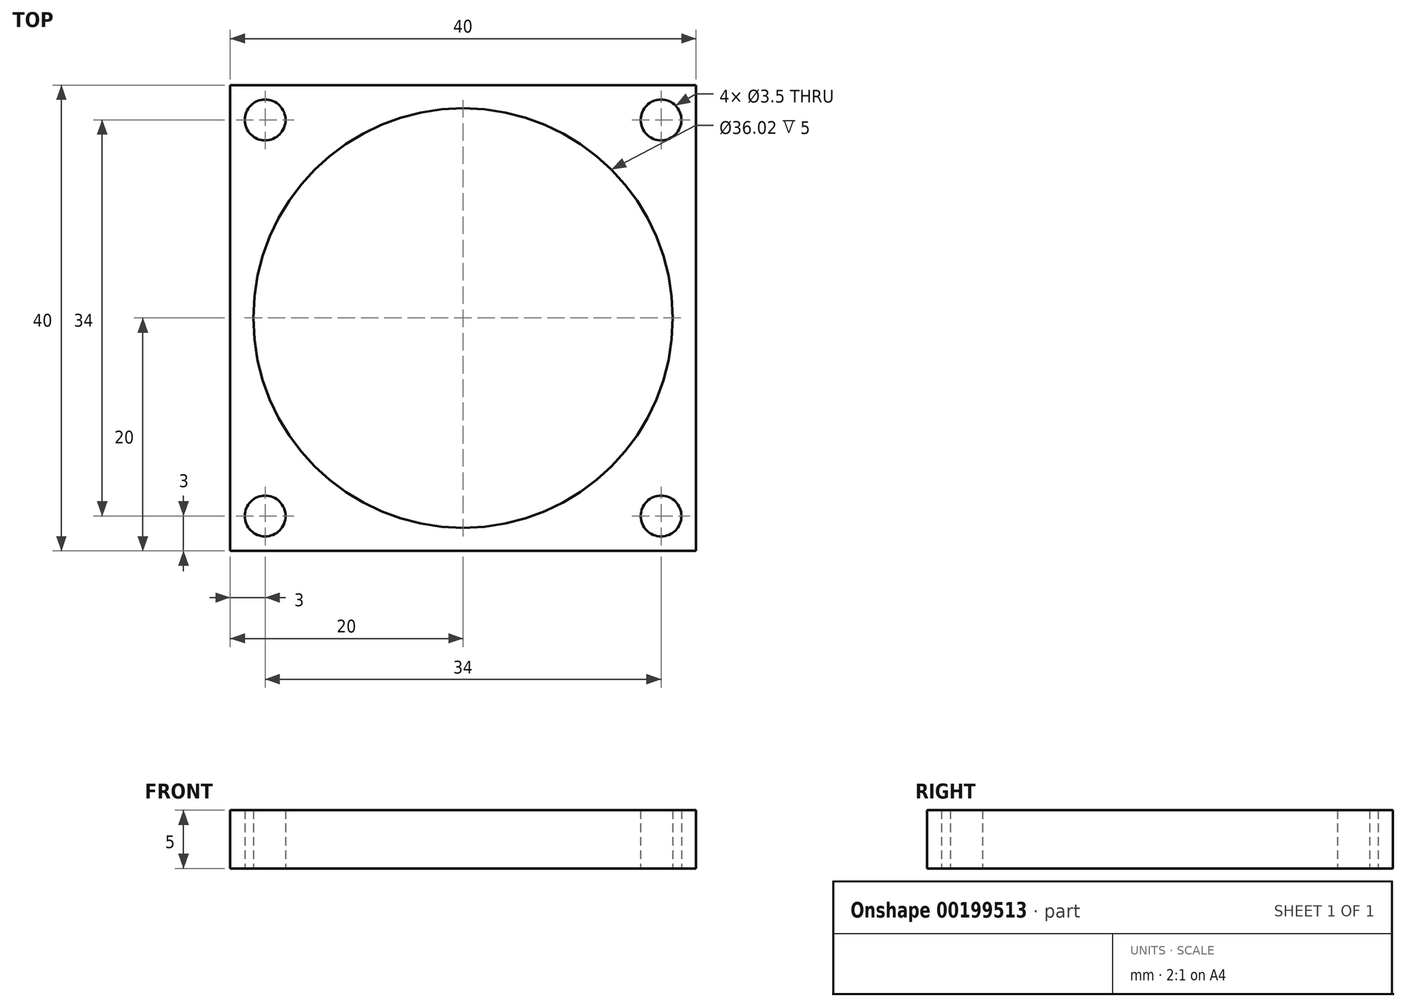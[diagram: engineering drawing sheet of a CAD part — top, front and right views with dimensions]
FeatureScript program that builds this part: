
annotation { "Feature Type Name" : "Feature", "Feature Type Description" : "" }
export const myFeature = defineFeature(function(context is Context, id is Id, definition is map)
    precondition{}
    {
        {
            var Q0;
            Q0=qCreatedBy(makeId("Top.planeOp"),FACE);
            var sketch = newSketch(context, id + "F0", { "sketchPlane" : qUnion([Q0])});
            skLineSegment(sketch, "E0.bottom", {"start": v(20, 20) * mm, "end": v(-20, 20) * mm});
            skLineSegment(sketch, "E0.top", {"start": v(20, -20) * mm, "end": v(-20, -20) * mm});
            skLineSegment(sketch, "E0.left", {"start": v(20, 20) * mm, "end": v(20, -20) * mm});
            skLineSegment(sketch, "E0.right", {"start": v(-20, 20) * mm, "end": v(-20, -20) * mm});
            skPoint(sketch, "E0.middle", {"position": v(0, 0) * mm});
            skLineSegment(sketch, "E1.bottom", {"start": v(17, 17) * mm, "end": v(-17, 17) * mm});
            skLineSegment(sketch, "E1.top", {"start": v(17, -17) * mm, "end": v(-17, -17) * mm});
            skLineSegment(sketch, "E1.left", {"start": v(17, 17) * mm, "end": v(17, -17) * mm});
            skLineSegment(sketch, "E1.right", {"start": v(-17, 17) * mm, "end": v(-17, -17) * mm});
            skCircle(sketch, "E2", {"center": v(-17, 17) * mm, "radius": 1.75 * mm});
            skCircle(sketch, "E3", {"center": v(17, 17) * mm, "radius": 1.75 * mm});
            skCircle(sketch, "E4", {"center": v(17, -17) * mm, "radius": 1.75 * mm});
            skCircle(sketch, "E5", {"center": v(-17, -17) * mm, "radius": 1.75 * mm});
            skCircle(sketch, "E6", {"center": v(0, 0) * mm, "radius": 18.01 * mm});
            skSolve(sketch);
        }
        {
            var Q0;
            Q0 = qSketchRegion(id + "F0", true);
            var Q1;
            {var subQ0=sQuery(id+"F0.wireOp",EDGE,"E6");var subQ1=sQuery(id+"F0.wireOp",EDGE,"E1.top");var subQ2=makeQuery(id+"F0.imprint","INTERSECT",VERTEX,{"disambiguationData":[OD(1.0)],"derivedFrom":[subQ1,subQ0]});Q1=makeQuery(id+"F0.imprint","IMPRINT",FACE,{"disambiguationData":[TD([[makeQuery(id+"F0.imprint","IMPRINT",EDGE,{"disambiguationData":[TD([[subQ2,-1.0]])],"derivedFrom":subQ1}),-1.0]])]});}
            var Q2;
            {var subQ0=sQuery(id+"F0.wireOp",EDGE,"E6");var subQ1=sQuery(id+"F0.wireOp",EDGE,"E1.bottom");var subQ2=makeQuery(id+"F0.imprint","INTERSECT",VERTEX,{"disambiguationData":[OD(1.0)],"derivedFrom":[subQ1,subQ0]});Q2=makeQuery(id+"F0.imprint","IMPRINT",FACE,{"disambiguationData":[TD([[makeQuery(id+"F0.imprint","IMPRINT",EDGE,{"disambiguationData":[TD([[subQ2,-1.0]])],"derivedFrom":subQ1}),1.0]])]});}
            var Q3;
            {var subQ0=sQuery(id+"F0.wireOp",EDGE,"E3");var subQ1=sQuery(id+"F0.wireOp",EDGE,"E1.bottom");var subQ2=makeQuery(id+"F0.imprint","INTERSECT",VERTEX,{"derivedFrom":[subQ1,subQ0]});Q3=makeQuery(id+"F0.imprint","IMPRINT",FACE,{"disambiguationData":[TD([[makeQuery(id+"F0.imprint","IMPRINT",EDGE,{"disambiguationData":[TD([[subQ2,-1.0]])],"derivedFrom":subQ1}),1.0]])]});}
            var Q4;
            {var subQ0=sQuery(id+"F0.wireOp",EDGE,"E4");var subQ1=sQuery(id+"F0.wireOp",EDGE,"E1.top");var subQ2=makeQuery(id+"F0.imprint","INTERSECT",VERTEX,{"derivedFrom":[subQ1,subQ0]});Q4=makeQuery(id+"F0.imprint","IMPRINT",FACE,{"disambiguationData":[TD([[makeQuery(id+"F0.imprint","IMPRINT",EDGE,{"disambiguationData":[TD([[subQ2,-1.0]])],"derivedFrom":subQ1}),-1.0]])]});}
            extrude(context, id + "F1", {"entities" : qUnion([Q0, Q1, Q2, Q3, Q4]), "depth" : 5 * mm});
        }
    });
